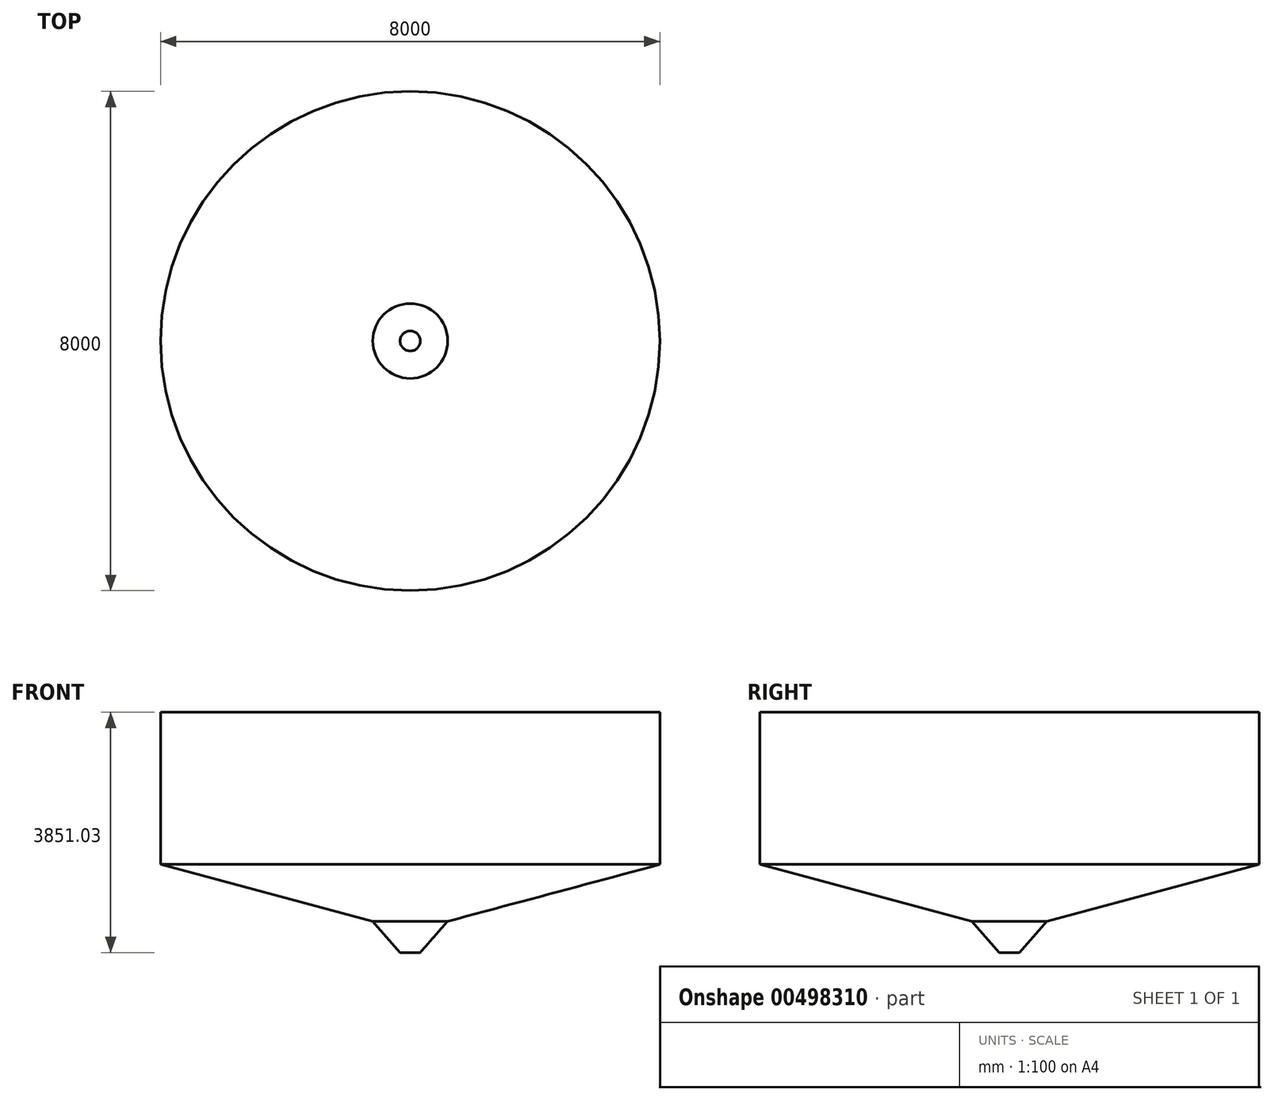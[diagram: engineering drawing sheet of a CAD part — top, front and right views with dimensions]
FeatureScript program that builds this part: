
annotation { "Feature Type Name" : "Feature", "Feature Type Description" : "" }
export const myFeature = defineFeature(function(context is Context, id is Id, definition is map)
    precondition{}
    {
        {
            var Q0;
            Q0=qCreatedBy(makeId("Front.planeOp"),FACE);
            var sketch = newSketch(context, id + "F0", { "sketchPlane" : qUnion([Q0])});
            skLineSegment(sketch, "E0", {"start": v(0, 0) * mm, "end": v(0, 2440) * mm, "construction": true});
            skLineSegment(sketch, "E1", {"start": v(4000, 2440) * mm, "end": v(4000, 0) * mm});
            skLineSegment(sketch, "E2", {"start": v(4000, 0) * mm, "end": v(600, -911.03) * mm});
            skLineSegment(sketch, "E3", {"start": v(600, -911.03) * mm, "end": v(162, -1411.03) * mm});
            skLineSegment(sketch, "E4", {"start": v(600, -911.03) * mm, "end": v(2459.74, -911.03) * mm, "construction": true});
            skSolve(sketch);
        }
        {
            var Q0;
            Q0 = qSketchRegion(id + "F0", true);
            var Q1;
            Q1=sQuery(id+"F0.wireOp",EDGE,"E3");
            var Q2;
            Q2=sQuery(id+"F0.wireOp",EDGE,"E2");
            var Q3;
            Q3=sQuery(id+"F0.wireOp",EDGE,"E1");
            var Q4;
            Q4=sQuery(id+"F0.wireOp",EDGE,"E0");
            revolve(context, id + "F1", {"bodyType" : ToolBodyType.SURFACE, "entities" : qUnion([Q0]), "surfaceEntities" : qUnion([Q1, Q2, Q3]), "axis" : qUnion([Q4]), "revolveType" : RevolveType.FULL});
        }
    });
